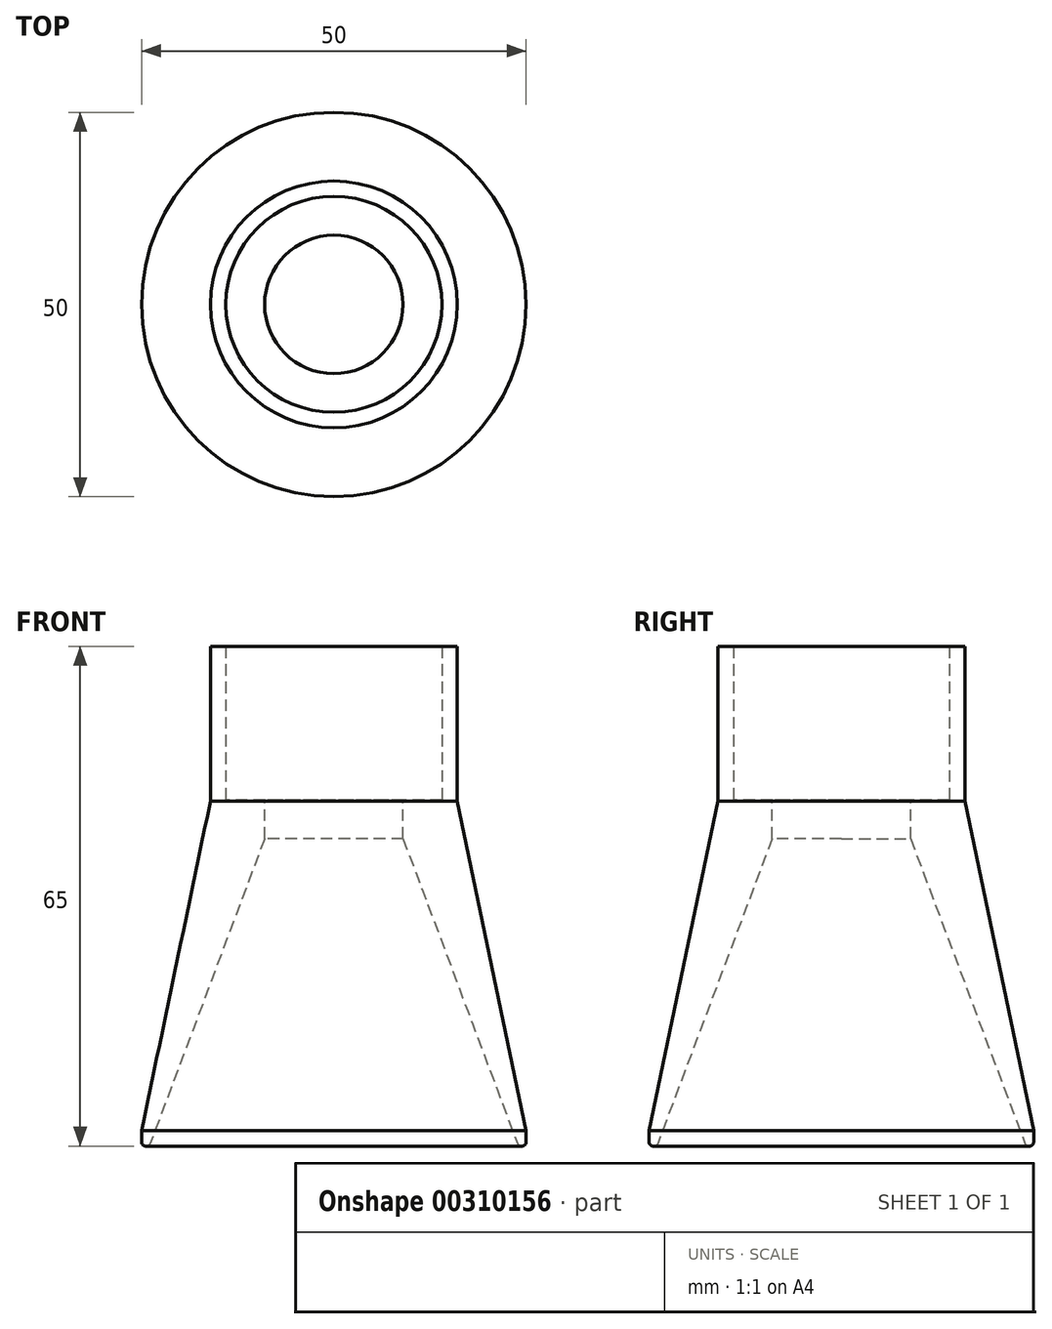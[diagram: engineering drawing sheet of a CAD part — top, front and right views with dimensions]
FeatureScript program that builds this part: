
annotation { "Feature Type Name" : "Feature", "Feature Type Description" : "" }
export const myFeature = defineFeature(function(context is Context, id is Id, definition is map)
    precondition{}
    {
        {
            var Q0;
            Q0=qCreatedBy(makeId("Top.planeOp"),FACE);
            var sketch = newSketch(context, id + "F0", { "sketchPlane" : qUnion([Q0])});
            skCircle(sketch, "E0", {"center": v(0, 0) * mm, "radius": 14.05 * mm});
            skCircle(sketch, "E1", {"center": v(0, 0) * mm, "radius": 8.85 * mm});
            skCircle(sketch, "E2", {"center": v(0, 0) * mm, "radius": 16.05 * mm});
            skSolve(sketch);
        }
        {
            var Q0;
            Q0 = qSketchRegion(id + "F0", true);
            var Q1;
            Q1=makeQuery(id+"F0.imprint","IMPRINT",FACE,{"disambiguationData":[TD([[makeQuery(id+"F0.imprint","IMPRINT",EDGE,{"derivedFrom":sQuery(id+"F0.wireOp",EDGE,"ZtDScnWZ-ek5Q-Wyjc-t4o0-LRsXn3DrjWyD")}),-1.0]])]});
            var Q2;
            Q2=makeQuery(id+"F0.imprint","IMPRINT",FACE,{"disambiguationData":[TD([[makeQuery(id+"F0.imprint","IMPRINT",EDGE,{"derivedFrom":sQuery(id+"F0.wireOp",EDGE,"vb3HU9EW-MXSu-EFM6-jFuB-Yvf3zv0E0FyK")}),1.0]])]});
            extrude(context, id + "F1", {"entities" : qUnion([Q0, Q1, Q2]), "depth" : 40 * mm});
        }
        {
            var Q0;
            Q0=makeQuery(id+"F1.opExtrude","CAP_FACE",FACE,{"disambiguationData":[OSD([sQuery(id+"F0.wireOp",EDGE,"E0"),sQuery(id+"F0.wireOp",EDGE,"ZtDScnWZ-ek5Q-Wyjc-t4o0-LRsXn3DrjWyD")])],"isStart":true});
            var sketch = newSketch(context, id + "F2", { "sketchPlane" : qUnion([Q0])});
            skCircle(sketch, "E3", {"center": v(0, 0) * mm, "radius": 25 * mm});
            skCircle(sketch, "E4", {"center": v(0, 0) * mm, "radius": 23 * mm});
            skSolve(sketch);
        }
        {
            var Q0;
            Q0=makeQuery(id+"F2.imprint","IMPRINT",FACE,{"disambiguationData":[TD([[makeQuery(id+"F2.imprint","IMPRINT",EDGE,{"derivedFrom":makeQuery(id+"F1.opExtrude","CAP_EDGE",EDGE,{"disambiguationData":[OSD([sQuery(id+"F0.wireOp",EDGE,"E0")])],"isStart":true})}),1.0]])]});
            var Q1;
            Q1=makeQuery(id+"F2.imprint","IMPRINT",FACE,{"disambiguationData":[TD([[makeQuery(id+"F2.imprint","IMPRINT",EDGE,{"derivedFrom":sQuery(id+"F2.wireOp",EDGE,"E3")}),1.0]])]});
            var Q2;
            Q2=makeQuery(id+"F2.imprint","IMPRINT",FACE,{"disambiguationData":[TD([[makeQuery(id+"F2.imprint","IMPRINT",EDGE,{"derivedFrom":sQuery(id+"F2.wireOp",EDGE,"E4")}),1.0]])]});
            extrude(context, id + "F3", {"entities" : qUnion([Q0, Q1, Q2]), "operationType" : NewBodyOperationType.ADD, "depth" : 25 * mm});
        }
        {
            var Q0;
            Q0=makeQuery(id+"F3.opExtrude","CAP_FACE",FACE,{"disambiguationData":[OSD([sQuery(id+"F0.wireOp",EDGE,"E0"),sQuery(id+"F2.wireOp",EDGE,"E3")])],"isStart":true});
            extrude(context, id + "F4", {"entities" : qUnion([Q0]), "operationType" : NewBodyOperationType.ADD, "depth" : 20 * mm});
        }
        {
            var Q0;
            Q0=makeQuery(id+"F4.opExtrude","CAP_EDGE",EDGE,{"disambiguationData":[OSD([sQuery(id+"F2.wireOp",EDGE,"E3")])],"isStart":false});
            chamfer(context, id + "F5", {"entities" : qUnion([Q0]), "chamferType" : ChamferType.OFFSET_ANGLE, "width" : 43 * mm, "oppositeDirection" : false, "angle" : 11.8 * degree, "tangentPropagation" : true});
        }
        {
            var Q0;
            Q0=qCreatedBy(makeId("Top.planeOp"),FACE);
            cPlane(context, id + "F6", {"entities" : qUnion([Q0]), "cplaneType" : CPlaneType.OFFSET, "offset" : 20 * mm, "width" : 150 * mm, "height" : 150 * mm});
        }
        {
            var Q0;
            Q0=qCreatedBy(id+"F6.planeOp",FACE);
            var sketch = newSketch(context, id + "F7", { "sketchPlane" : qUnion([Q0])});
            skCircle(sketch, "E5", {"center": v(0, 0) * mm, "radius": 9 * mm});
            skCircle(sketch, "E6", {"center": v(0, 0) * mm, "radius": 15 * mm});
            skSolve(sketch);
        }
        {
            var Q0;
            Q0=makeQuery(id+"F7.imprint","IMPRINT",FACE,{"disambiguationData":[TD([[makeQuery(id+"F7.imprint","IMPRINT",EDGE,{"derivedFrom":sQuery(id+"F7.wireOp",EDGE,"E5")}),-1.0]])]});
            extrude(context, id + "F8", {"entities" : qUnion([Q0]), "operationType" : NewBodyOperationType.ADD, "depth" : -45 * mm});
        }
        {
            var Q0;
            Q0=makeQuery(id+"F8.opExtrude","CAP_EDGE",EDGE,{"disambiguationData":[OSD([sQuery(id+"F7.wireOp",EDGE,"E5")])],"isStart":false});
            chamfer(context, id + "F9", {"entities" : qUnion([Q0]), "chamferType" : ChamferType.TWO_OFFSETS, "width1" : 15 * mm, "oppositeDirection" : false, "width2" : 40 * mm, "tangentPropagation" : true});
        }
        {
            var Q0;
            Q0=makeQuery(id+"F8.boolean.opBoolean","MERGE",FACE,{"derivedFrom":[makeQuery(id+"F3.opExtrude","CAP_FACE",FACE,{"disambiguationData":[OSD([sQuery(id+"F0.wireOp",EDGE,"E0"),sQuery(id+"F2.wireOp",EDGE,"E3")])],"isStart":false}),makeQuery(id+"F8.opExtrude","CAP_FACE",FACE,{"disambiguationData":[OSD([sQuery(id+"F7.wireOp",EDGE,"E5"),sQuery(id+"F7.wireOp",EDGE,"E6")])],"isStart":false})]});
            fillet(context, id + "F10", {"entities" : qUnion([Q0]), "radius" : 0.5 * mm, "tangentPropagation" : true, "allowEdgeOverflow" : false});
        }
    });
